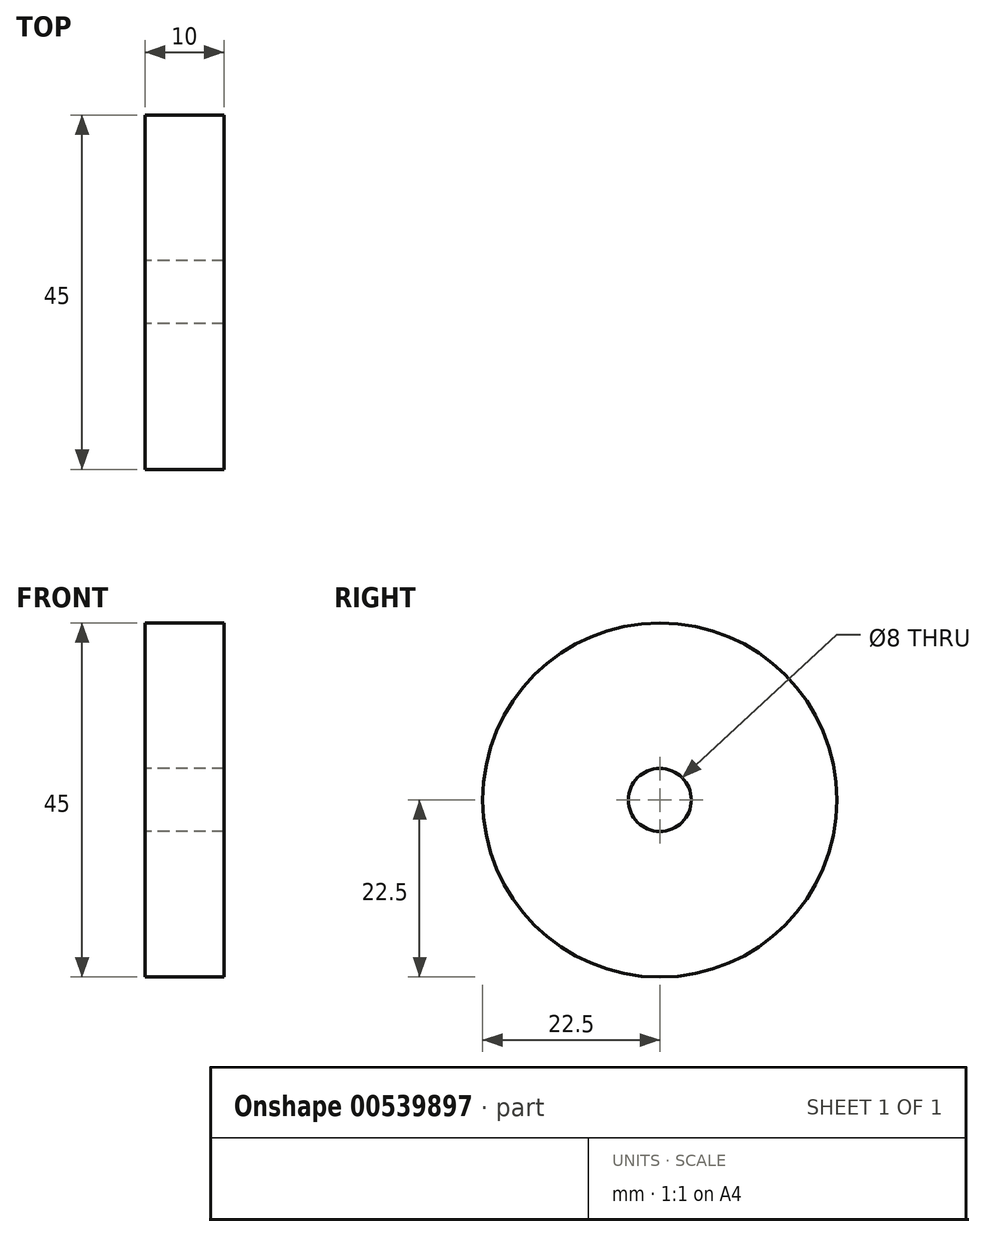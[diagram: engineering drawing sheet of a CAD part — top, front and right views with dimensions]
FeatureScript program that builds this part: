
annotation { "Feature Type Name" : "Feature", "Feature Type Description" : "" }
export const myFeature = defineFeature(function(context is Context, id is Id, definition is map)
    precondition{}
    {
        {
            var Q0;
            Q0=qCreatedBy(makeId("Right.planeOp"),FACE);
            var sketch = newSketch(context, id + "F0", { "sketchPlane" : qUnion([Q0])});
            skCircle(sketch, "E0", {"center": v(0, 0) * mm, "radius": 4 * mm});
            skCircle(sketch, "E1", {"center": v(0, 0) * mm, "radius": 22.5 * mm});
            skSolve(sketch);
        }
        {
            var Q0;
            Q0 = qSketchRegion(id + "F0", true);
            extrude(context, id + "F1", {"entities" : qUnion([Q0]), "depth" : 10 * mm, "offsetDistance" : 25 * mm});
        }
    });
